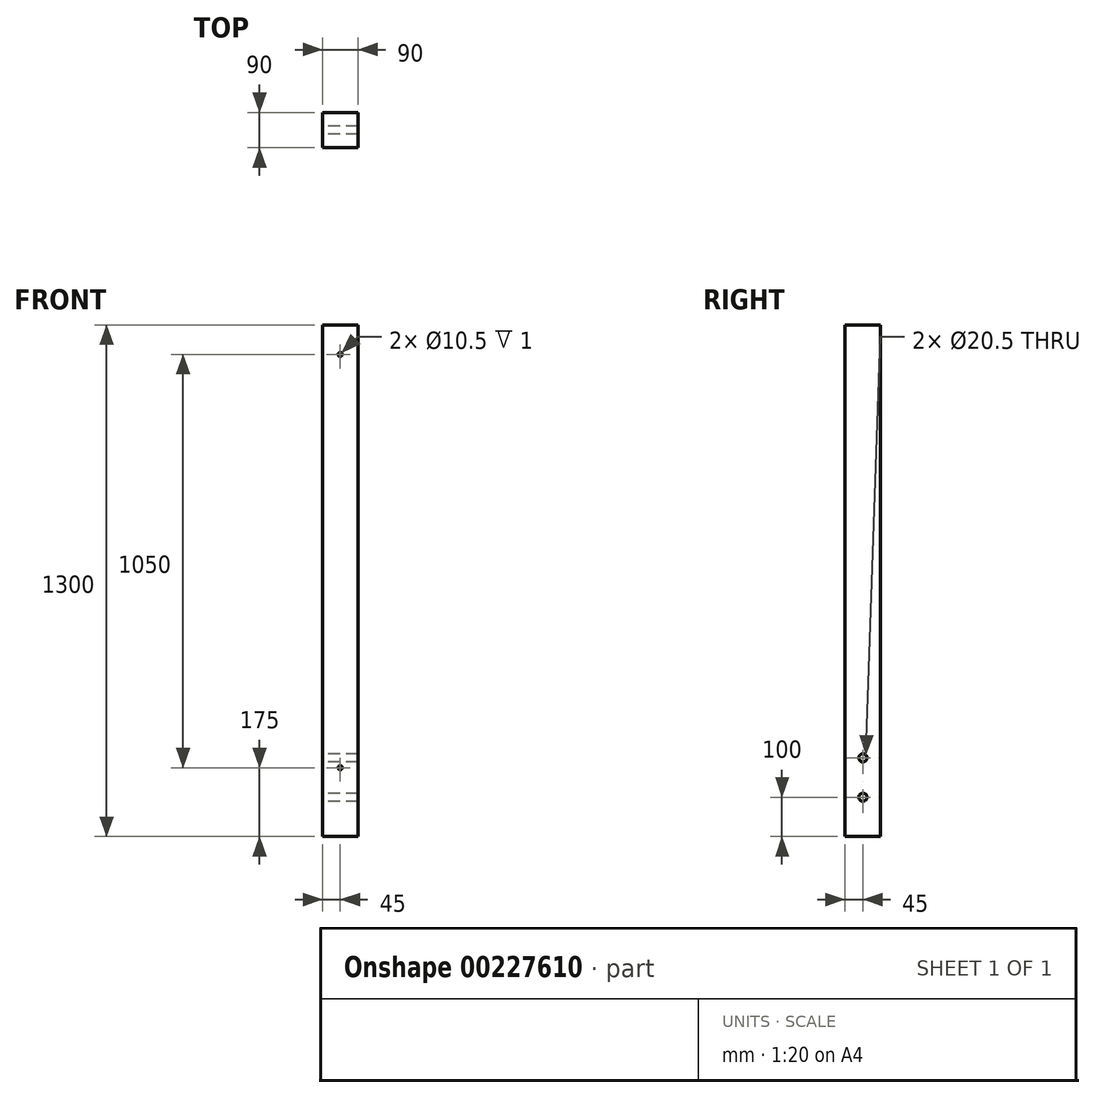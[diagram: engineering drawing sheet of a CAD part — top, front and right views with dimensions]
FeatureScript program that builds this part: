
annotation { "Feature Type Name" : "Feature", "Feature Type Description" : "" }
export const myFeature = defineFeature(function(context is Context, id is Id, definition is map)
    precondition{}
    {
        {
            var Q0;
            Q0=qCreatedBy(makeId("Top.planeOp"),FACE);
            var sketch = newSketch(context, id + "F0", { "sketchPlane" : qUnion([Q0])});
            skLineSegment(sketch, "E0.bottom", {"start": v(45, 45) * mm, "end": v(-45, 45) * mm});
            skLineSegment(sketch, "E0.top", {"start": v(45, -45) * mm, "end": v(-45, -45) * mm});
            skLineSegment(sketch, "E0.left", {"start": v(45, 45) * mm, "end": v(45, -45) * mm});
            skLineSegment(sketch, "E0.right", {"start": v(-45, 45) * mm, "end": v(-45, -45) * mm});
            skPoint(sketch, "E0.middle", {"position": v(0, 0) * mm});
            skSolve(sketch);
        }
        {
            var Q0;
            Q0 = qSketchRegion(id + "F0", true);
            extrude(context, id + "F1", {"entities" : qUnion([Q0]), "depth" : 1300 * mm});
        }
        {
            var Q0;
            Q0=makeQuery(id+"F1.opExtrude","SWEPT_FACE",FACE,{"disambiguationData":[OSD([sQuery(id+"F0.wireOp",EDGE,"E0.top")])]});
            var sketch = newSketch(context, id + "F2", { "sketchPlane" : qUnion([Q0])});
            skLineSegment(sketch, "E1", {"start": v(0, 1300) * mm, "end": v(0, -6.33) * mm, "construction": true});
            skCircle(sketch, "E2", {"center": v(0, 1225) * mm, "radius": 5.25 * mm});
            skCircle(sketch, "E3", {"center": v(0, 175) * mm, "radius": 5.25 * mm});
            skSolve(sketch);
        }
        {
            var Q0;
            Q0 = qSketchRegion(id + "F2", true);
            extrude(context, id + "F3", {"entities" : qUnion([Q0]), "operationType" : NewBodyOperationType.REMOVE, "oppositeDirection" : true, "depth" : 1 * mm});
        }
        {
            var Q0;
            Q0=makeQuery(id+"F1.opExtrude","SWEPT_FACE",FACE,{"disambiguationData":[OSD([sQuery(id+"F0.wireOp",EDGE,"E0.right")])]});
            var sketch = newSketch(context, id + "F4", { "sketchPlane" : qUnion([Q0])});
            skLineSegment(sketch, "E4", {"start": v(0, 0) * mm, "end": v(0, 1300) * mm, "construction": true});
            skCircle(sketch, "E5", {"center": v(0, 100) * mm, "radius": 10.25 * mm});
            skCircle(sketch, "E6", {"center": v(0, 200) * mm, "radius": 10.25 * mm});
            skSolve(sketch);
        }
        {
            var Q0;
            Q0 = qSketchRegion(id + "F4", true);
            extrude(context, id + "F5", {"entities" : qUnion([Q0]), "operationType" : NewBodyOperationType.REMOVE, "endBound" : BoundingType.THROUGH_ALL, "oppositeDirection" : true, "depth" : 25 * mm});
        }
    });
